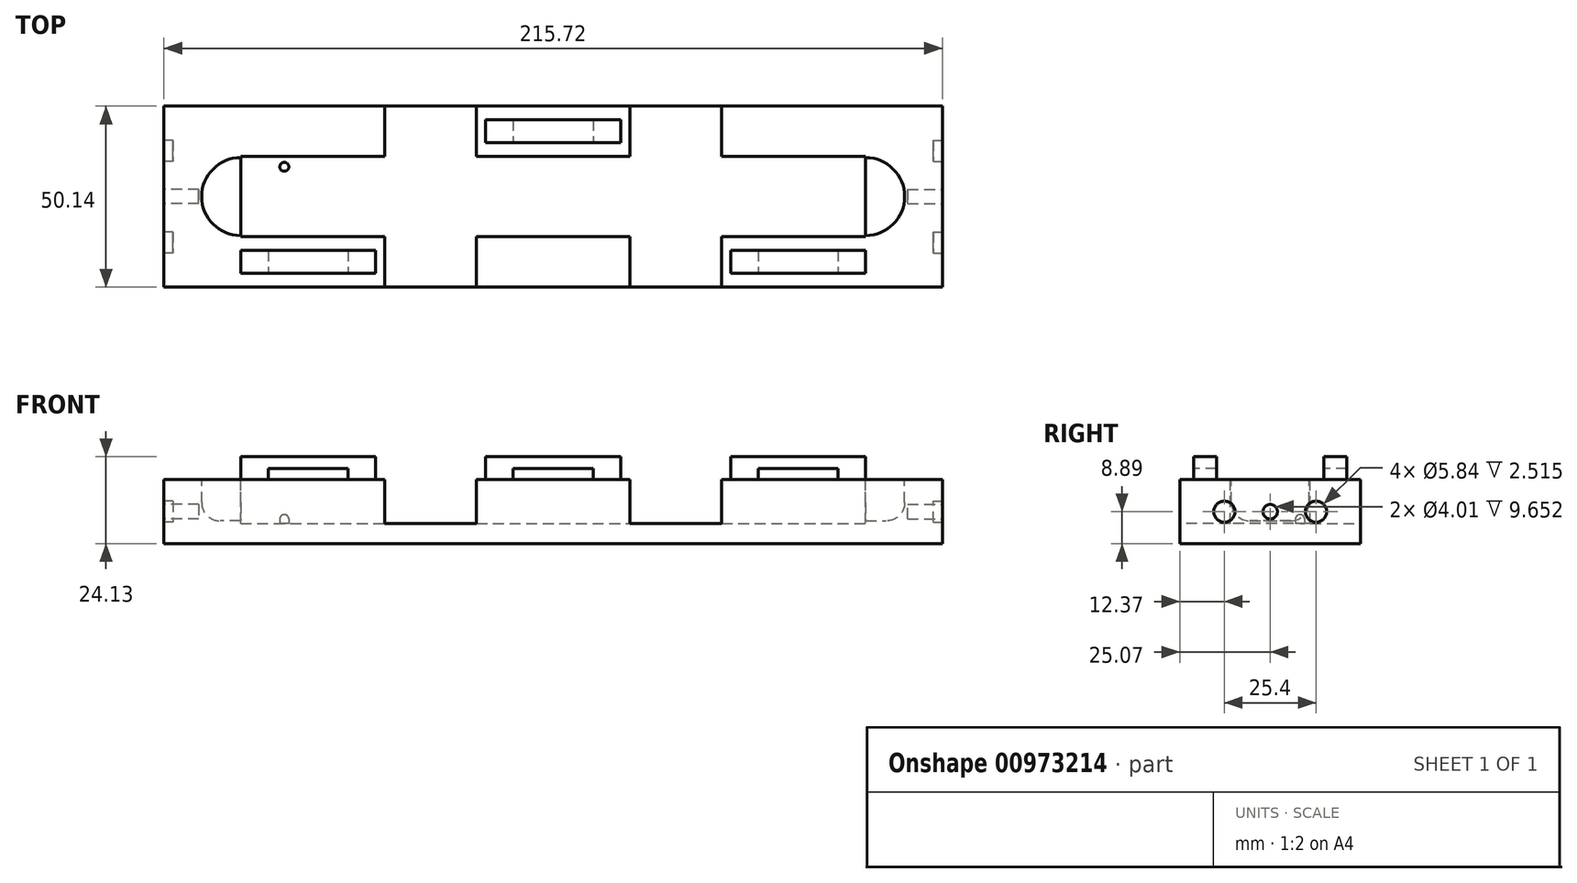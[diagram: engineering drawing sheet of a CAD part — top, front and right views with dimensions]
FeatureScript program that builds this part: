
annotation { "Feature Type Name" : "Feature", "Feature Type Description" : "" }
export const myFeature = defineFeature(function(context is Context, id is Id, definition is map)
    precondition{}
    {
        {
            var Q0;
            Q0=qCreatedBy(makeId("Top.planeOp"),FACE);
            var sketch = newSketch(context, id + "F0", { "sketchPlane" : qUnion([Q0])});
            skLineSegment(sketch, "E0.bottom", {"start": v(-107.86, 25.07) * mm, "end": v(107.86, 25.07) * mm});
            skLineSegment(sketch, "E0.top", {"start": v(-107.86, -25.07) * mm, "end": v(107.86, -25.07) * mm});
            skLineSegment(sketch, "E0.left", {"start": v(-107.86, 25.07) * mm, "end": v(-107.86, -25.07) * mm});
            skLineSegment(sketch, "E0.right", {"start": v(107.86, 25.07) * mm, "end": v(107.86, -25.07) * mm});
            skPoint(sketch, "E0.middle", {"position": v(0, 0) * mm});
            skSolve(sketch);
        }
        {
            var Q0;
            Q0=makeQuery(id+"F0.imprint","IMPRINT",FACE,{"disambiguationData":[TD([[makeQuery(id+"F0.imprint","IMPRINT",EDGE,{"derivedFrom":sQuery(id+"F0.wireOp",EDGE,"E0.bottom")}),-1.0]])]});
            extrude(context, id + "F1", {"entities" : qUnion([Q0]), "depth" : 17.78 * mm, "offsetDistance" : 25.4 * mm});
        }
        {
            var Q0;
            Q0=makeQuery(id+"F1.opExtrude","CAP_FACE",FACE,{"disambiguationData":[OSD([sQuery(id+"F0.wireOp",EDGE,"E0.bottom"),sQuery(id+"F0.wireOp",EDGE,"E0.top"),sQuery(id+"F0.wireOp",EDGE,"E0.left"),sQuery(id+"F0.wireOp",EDGE,"E0.right")])],"isStart":false});
            var sketch = newSketch(context, id + "F2", { "sketchPlane" : qUnion([Q0])});
            skLineSegment(sketch, "E1.bottom", {"start": v(-86.6, 11.1) * mm, "end": v(86.6, 11.1) * mm});
            skLineSegment(sketch, "E1.top", {"start": v(-86.6, -11.1) * mm, "end": v(86.6, -11.1) * mm});
            skLineSegment(sketch, "E1.left", {"start": v(-86.6, 11.1) * mm, "end": v(-86.6, -11.1) * mm});
            skLineSegment(sketch, "E1.right", {"start": v(86.6, 11.1) * mm, "end": v(86.6, -11.1) * mm});
            skPoint(sketch, "E1.middle", {"position": v(0, 0) * mm});
            skSolve(sketch);
        }
        {
            var Q0;
            Q0=makeQuery(id+"F2.imprint","IMPRINT",FACE,{"disambiguationData":[TD([[makeQuery(id+"F2.imprint","IMPRINT",EDGE,{"derivedFrom":sQuery(id+"F2.wireOp",EDGE,"E1.bottom")}),-1.0]])]});
            extrude(context, id + "F3", {"entities" : qUnion([Q0]), "operationType" : NewBodyOperationType.REMOVE, "oppositeDirection" : true, "depth" : 12.2 * mm, "offsetDistance" : 25.4 * mm});
        }
        {
            var Q0;
            Q0=makeQuery(id+"F1.opExtrude","CAP_FACE",FACE,{"disambiguationData":[OSD([sQuery(id+"F0.wireOp",EDGE,"E0.bottom"),sQuery(id+"F0.wireOp",EDGE,"E0.top"),sQuery(id+"F0.wireOp",EDGE,"E0.left"),sQuery(id+"F0.wireOp",EDGE,"E0.right")])],"isStart":false});
            var sketch = newSketch(context, id + "F4", { "sketchPlane" : qUnion([Q0])});
            skCircle(sketch, "E2", {"center": v(-86.6, 0) * mm, "radius": 10.8 * mm});
            skCircle(sketch, "E3", {"center": v(86.6, 0) * mm, "radius": 10.8 * mm});
            skSolve(sketch);
        }
        {
            var Q0;
            {var subQ0=sQuery(id+"F4.wireOp",EDGE,"E2");var subQ1=makeQuery(id+"F3.boolean.opBoolean","COPY",EDGE,{"derivedFrom":makeQuery(id+"F3.opExtrude","CAP_EDGE",EDGE,{"disambiguationData":[OSD([sQuery(id+"F2.wireOp",EDGE,"E1.left")])],"isStart":true})});var subQ2=makeQuery(id+"F4.imprint","INTERSECT",VERTEX,{"disambiguationData":[OD(0.0)],"derivedFrom":[subQ1,subQ0]});Q0=makeQuery(id+"F4.imprint","IMPRINT",FACE,{"disambiguationData":[TD([[makeQuery(id+"F4.imprint","IMPRINT",EDGE,{"disambiguationData":[TD([[subQ2,-1.0]])],"derivedFrom":subQ0}),1.0]])]});}
            var Q1;
            {var subQ0=sQuery(id+"F4.wireOp",EDGE,"7IIQq3Zt-Aci2-6bUa-GBsR-gUbxx56y20vS");var subQ1=makeQuery(id+"F3.boolean.opBoolean","COPY",EDGE,{"derivedFrom":makeQuery(id+"F3.opExtrude","CAP_EDGE",EDGE,{"disambiguationData":[OSD([sQuery(id+"F2.wireOp",EDGE,"E1.bottom")])],"isStart":true})});var subQ2=makeQuery(id+"F4.imprint","INTERSECT",VERTEX,{"disambiguationData":[OD(0.0)],"derivedFrom":[subQ1,subQ0]});Q1=makeQuery(id+"F4.imprint","IMPRINT",FACE,{"disambiguationData":[TD([[makeQuery(id+"F4.imprint","IMPRINT",EDGE,{"disambiguationData":[TD([[subQ2,1.0]])],"derivedFrom":subQ0}),1.0]])]});}
            var Q2;
            {var subQ0=sQuery(id+"F4.wireOp",EDGE,"ctRysrec-sLNG-mFqm-rWU9-T6cm6gCdLbKU");var subQ1=makeQuery(id+"F3.boolean.opBoolean","COPY",EDGE,{"derivedFrom":makeQuery(id+"F3.opExtrude","CAP_EDGE",EDGE,{"disambiguationData":[OSD([sQuery(id+"F2.wireOp",EDGE,"E1.top")])],"isStart":true})});var subQ2=makeQuery(id+"F4.imprint","INTERSECT",VERTEX,{"disambiguationData":[OD(0.0)],"derivedFrom":[subQ1,subQ0]});Q2=makeQuery(id+"F4.imprint","IMPRINT",FACE,{"disambiguationData":[TD([[makeQuery(id+"F4.imprint","IMPRINT",EDGE,{"disambiguationData":[TD([[subQ2,1.0]])],"derivedFrom":subQ0}),1.0]])]});}
            var Q3;
            {var subQ0=sQuery(id+"F4.wireOp",EDGE,"WosAOIdG-twBO-UutL-H2nZ-O1rzlQHSEw63");var subQ1=makeQuery(id+"F3.boolean.opBoolean","COPY",EDGE,{"derivedFrom":makeQuery(id+"F3.opExtrude","CAP_EDGE",EDGE,{"disambiguationData":[OSD([sQuery(id+"F2.wireOp",EDGE,"E1.bottom")])],"isStart":true})});var subQ2=makeQuery(id+"F4.imprint","INTERSECT",VERTEX,{"disambiguationData":[OD(0.0)],"derivedFrom":[subQ1,subQ0]});Q3=makeQuery(id+"F4.imprint","IMPRINT",FACE,{"disambiguationData":[TD([[makeQuery(id+"F4.imprint","IMPRINT",EDGE,{"disambiguationData":[TD([[subQ2,1.0]])],"derivedFrom":subQ0}),1.0]])]});}
            var Q4;
            {var subQ0=sQuery(id+"F4.wireOp",EDGE,"E3");var subQ1=makeQuery(id+"F3.boolean.opBoolean","COPY",EDGE,{"derivedFrom":makeQuery(id+"F3.opExtrude","CAP_EDGE",EDGE,{"disambiguationData":[OSD([sQuery(id+"F2.wireOp",EDGE,"E1.right")])],"isStart":true})});var subQ2=makeQuery(id+"F4.imprint","INTERSECT",VERTEX,{"disambiguationData":[OD(0.0)],"derivedFrom":[subQ1,subQ0]});Q4=makeQuery(id+"F4.imprint","IMPRINT",FACE,{"disambiguationData":[TD([[makeQuery(id+"F4.imprint","IMPRINT",EDGE,{"disambiguationData":[TD([[subQ2,1.0]])],"derivedFrom":subQ0}),1.0]])]});}
            var Q5;
            {var subQ0=sQuery(id+"F4.wireOp",EDGE,"np94UB7D-fCDP-aEEe-Vjp5-RGfSFigQMC2d");var subQ1=makeQuery(id+"F3.boolean.opBoolean","COPY",EDGE,{"derivedFrom":makeQuery(id+"F3.opExtrude","CAP_EDGE",EDGE,{"disambiguationData":[OSD([sQuery(id+"F2.wireOp",EDGE,"E1.top")])],"isStart":true})});var subQ2=makeQuery(id+"F4.imprint","INTERSECT",VERTEX,{"disambiguationData":[OD(0.0)],"derivedFrom":[subQ1,subQ0]});Q5=makeQuery(id+"F4.imprint","IMPRINT",FACE,{"disambiguationData":[TD([[makeQuery(id+"F4.imprint","IMPRINT",EDGE,{"disambiguationData":[TD([[subQ2,1.0]])],"derivedFrom":subQ0}),1.0]])]});}
            extrude(context, id + "F5", {"entities" : qUnion([Q0, Q1, Q2, Q3, Q4, Q5]), "operationType" : NewBodyOperationType.REMOVE, "oppositeDirection" : true, "depth" : 11.43 * mm, "offsetDistance" : 25.4 * mm});
        }
        {
            var Q0;
            Q0=makeQuery(id+"F5.boolean.opBoolean","COPY",EDGE,{"derivedFrom":makeQuery(id+"F5.opExtrude","CAP_EDGE",EDGE,{"disambiguationData":[OSD([sQuery(id+"F4.wireOp",EDGE,"E2")])],"isStart":false})});
            var Q1;
            Q1=makeQuery(id+"F5.boolean.opBoolean","COPY",EDGE,{"derivedFrom":makeQuery(id+"F5.opExtrude","CAP_EDGE",EDGE,{"disambiguationData":[OSD([sQuery(id+"F4.wireOp",EDGE,"7IIQq3Zt-Aci2-6bUa-GBsR-gUbxx56y20vS")])],"isStart":false})});
            var Q2;
            Q2=makeQuery(id+"F5.boolean.opBoolean","COPY",EDGE,{"derivedFrom":makeQuery(id+"F5.opExtrude","CAP_EDGE",EDGE,{"disambiguationData":[OSD([sQuery(id+"F4.wireOp",EDGE,"ctRysrec-sLNG-mFqm-rWU9-T6cm6gCdLbKU")])],"isStart":false})});
            var Q3;
            Q3=makeQuery(id+"F5.boolean.opBoolean","COPY",EDGE,{"derivedFrom":makeQuery(id+"F5.opExtrude","CAP_EDGE",EDGE,{"disambiguationData":[OSD([sQuery(id+"F4.wireOp",EDGE,"WosAOIdG-twBO-UutL-H2nZ-O1rzlQHSEw63")])],"isStart":false})});
            var Q4;
            Q4=makeQuery(id+"F5.boolean.opBoolean","COPY",EDGE,{"derivedFrom":makeQuery(id+"F5.opExtrude","CAP_EDGE",EDGE,{"disambiguationData":[OSD([sQuery(id+"F4.wireOp",EDGE,"E3")])],"isStart":false})});
            var Q5;
            Q5=makeQuery(id+"F5.boolean.opBoolean","COPY",EDGE,{"derivedFrom":makeQuery(id+"F5.opExtrude","CAP_EDGE",EDGE,{"disambiguationData":[OSD([sQuery(id+"F4.wireOp",EDGE,"np94UB7D-fCDP-aEEe-Vjp5-RGfSFigQMC2d")])],"isStart":false})});
            fillet(context, id + "F6", {"entities" : qUnion([Q0, Q1, Q2, Q3, Q4, Q5]), "radius" : 5.08 * mm, "tangentPropagation" : true, "allowEdgeOverflow" : false});
        }
        {
            var Q0;
            Q0=makeQuery(id+"F3.boolean.opBoolean","COPY",FACE,{"derivedFrom":makeQuery(id+"F3.opExtrude","CAP_FACE",FACE,{"disambiguationData":[OSD([sQuery(id+"F2.wireOp",EDGE,"E1.bottom"),sQuery(id+"F2.wireOp",EDGE,"E1.top"),sQuery(id+"F2.wireOp",EDGE,"E1.left"),sQuery(id+"F2.wireOp",EDGE,"E1.right")])],"isStart":false})});
            var sketch = newSketch(context, id + "F7", { "sketchPlane" : qUnion([Q0])});
            skLineSegment(sketch, "E4.bottom", {"start": v(0, 11.1) * mm, "end": v(-74.5, 11.1) * mm});
            skLineSegment(sketch, "E4.top", {"start": v(0, 8.26) * mm, "end": v(-74.5, 8.25) * mm});
            skLineSegment(sketch, "E4.left", {"start": v(0, 11.1) * mm, "end": v(0, 8.26) * mm});
            skLineSegment(sketch, "E4.right", {"start": v(-74.5, 11.1) * mm, "end": v(-74.5, 8.25) * mm});
            skCircle(sketch, "E5", {"center": v(-74.5, 8.25) * mm, "radius": 1.24 * mm});
            skSolve(sketch);
        }
        {
            var Q0;
            {var subQ0=sQuery(id+"F7.wireOp",EDGE,"E4.right");var subQ1=sQuery(id+"F7.wireOp",EDGE,"E4.top");var subQ2=makeQuery(id+"F7.imprint","INTERSECT",VERTEX,{"derivedFrom":[subQ1,subQ0]});Q0=makeQuery(id+"F7.imprint","IMPRINT",FACE,{"disambiguationData":[TD([[makeQuery(id+"F7.imprint","IMPRINT",EDGE,{"disambiguationData":[TD([[subQ2,1.0]])],"derivedFrom":subQ1}),1.0]])]});}
            var Q1;
            {var subQ0=sQuery(id+"F7.wireOp",EDGE,"E4.right");var subQ1=sQuery(id+"F7.wireOp",EDGE,"E4.top");var subQ2=makeQuery(id+"F7.imprint","INTERSECT",VERTEX,{"derivedFrom":[subQ1,subQ0]});Q1=makeQuery(id+"F7.imprint","IMPRINT",FACE,{"disambiguationData":[TD([[makeQuery(id+"F7.imprint","IMPRINT",EDGE,{"disambiguationData":[TD([[subQ2,1.0]])],"derivedFrom":subQ1}),-1.0]])]});}
            extrude(context, id + "F8", {"entities" : qUnion([Q0, Q1]), "operationType" : NewBodyOperationType.ADD, "depth" : 2.5 * mm, "offsetDistance" : 25.4 * mm});
        }
        {
            var Q0;
            Q0=makeQuery(id+"F8.opExtrude","CAP_FACE",FACE,{"disambiguationData":[OSD([sQuery(id+"F7.wireOp",EDGE,"E5")])],"isStart":false});
            fillet(context, id + "F9", {"entities" : qUnion([Q0]), "radius" : 1.24 * mm, "tangentPropagation" : true, "allowEdgeOverflow" : false});
        }
        {
            var Q0;
            Q0=makeQuery(id+"F1.opExtrude","SWEPT_FACE",FACE,{"disambiguationData":[OSD([sQuery(id+"F0.wireOp",EDGE,"E0.right")])]});
            var sketch = newSketch(context, id + "F10", { "sketchPlane" : qUnion([Q0])});
            skCircle(sketch, "E6", {"center": v(0, 8.9) * mm, "radius": 2 * mm});
            skPoint(sketch, "E6.centerSnap0", {"position": v(0, 17.78) * mm});
            skSolve(sketch);
        }
        {
            var Q0;
            Q0=makeQuery(id+"F10.imprint","IMPRINT",FACE,{"disambiguationData":[TD([[makeQuery(id+"F10.imprint","IMPRINT",EDGE,{"derivedFrom":sQuery(id+"F10.wireOp",EDGE,"E6")}),1.0]])]});
            extrude(context, id + "F11", {"entities" : qUnion([Q0]), "operationType" : NewBodyOperationType.REMOVE, "oppositeDirection" : true, "depth" : 9.65 * mm, "offsetDistance" : 25.4 * mm});
        }
        {
            var Q0;
            Q0=makeQuery(id+"F1.opExtrude","SWEPT_FACE",FACE,{"disambiguationData":[OSD([sQuery(id+"F0.wireOp",EDGE,"E0.left")])]});
            var sketch = newSketch(context, id + "F12", { "sketchPlane" : qUnion([Q0])});
            skCircle(sketch, "E7", {"center": v(0, 8.9) * mm, "radius": 2 * mm});
            skSolve(sketch);
        }
        {
            var Q0;
            Q0=makeQuery(id+"F12.imprint","IMPRINT",FACE,{"disambiguationData":[TD([[makeQuery(id+"F12.imprint","IMPRINT",EDGE,{"derivedFrom":sQuery(id+"F12.wireOp",EDGE,"E7")}),1.0]])]});
            extrude(context, id + "F13", {"entities" : qUnion([Q0]), "operationType" : NewBodyOperationType.REMOVE, "oppositeDirection" : true, "depth" : 9.65 * mm, "offsetDistance" : 25.4 * mm});
        }
        {
            var Q0;
            Q0=makeQuery(id+"F1.opExtrude","SWEPT_FACE",FACE,{"disambiguationData":[OSD([sQuery(id+"F0.wireOp",EDGE,"E0.right")])]});
            var sketch = newSketch(context, id + "F14", { "sketchPlane" : qUnion([Q0])});
            skCircle(sketch, "E8", {"center": v(-12.7, 8.9) * mm, "radius": 2.92 * mm});
            skPoint(sketch, "E8.centerSnap0", {"position": v(-25.07, 8.9) * mm});
            skCircle(sketch, "E9", {"center": v(12.7, 8.9) * mm, "radius": 2.92 * mm});
            skPoint(sketch, "E9.centerSnap0", {"position": v(25.07, 8.9) * mm});
            skSolve(sketch);
        }
        {
            var Q0;
            Q0=makeQuery(id+"F14.imprint","IMPRINT",FACE,{"disambiguationData":[TD([[makeQuery(id+"F14.imprint","IMPRINT",EDGE,{"derivedFrom":sQuery(id+"F14.wireOp",EDGE,"E8")}),1.0]])]});
            var Q1;
            Q1=makeQuery(id+"F14.imprint","IMPRINT",FACE,{"disambiguationData":[TD([[makeQuery(id+"F14.imprint","IMPRINT",EDGE,{"derivedFrom":sQuery(id+"F14.wireOp",EDGE,"E9")}),1.0]])]});
            extrude(context, id + "F15", {"entities" : qUnion([Q0, Q1]), "operationType" : NewBodyOperationType.REMOVE, "oppositeDirection" : true, "depth" : 2.5 * mm, "offsetDistance" : 25.4 * mm});
        }
        {
            var Q0;
            Q0=makeQuery(id+"F1.opExtrude","SWEPT_FACE",FACE,{"disambiguationData":[OSD([sQuery(id+"F0.wireOp",EDGE,"E0.left")])]});
            var sketch = newSketch(context, id + "F16", { "sketchPlane" : qUnion([Q0])});
            skCircle(sketch, "E10", {"center": v(-12.7, 8.9) * mm, "radius": 2.92 * mm});
            skCircle(sketch, "E11", {"center": v(12.7, 8.9) * mm, "radius": 2.92 * mm});
            skPoint(sketch, "E11.centerSnap0", {"position": v(-25.07, 8.9) * mm});
            skSolve(sketch);
        }
        {
            var Q0;
            Q0=makeQuery(id+"F16.imprint","IMPRINT",FACE,{"disambiguationData":[TD([[makeQuery(id+"F16.imprint","IMPRINT",EDGE,{"derivedFrom":sQuery(id+"F16.wireOp",EDGE,"E10")}),1.0]])]});
            var Q1;
            Q1=makeQuery(id+"F16.imprint","IMPRINT",FACE,{"disambiguationData":[TD([[makeQuery(id+"F16.imprint","IMPRINT",EDGE,{"derivedFrom":sQuery(id+"F16.wireOp",EDGE,"E11")}),1.0]])]});
            extrude(context, id + "F17", {"entities" : qUnion([Q0, Q1]), "operationType" : NewBodyOperationType.REMOVE, "oppositeDirection" : true, "depth" : 2.5 * mm, "offsetDistance" : 25.4 * mm});
        }
        {
            var Q0;
            Q0=makeQuery(id+"F1.opExtrude","CAP_FACE",FACE,{"disambiguationData":[OSD([sQuery(id+"F0.wireOp",EDGE,"E0.bottom"),sQuery(id+"F0.wireOp",EDGE,"E0.top"),sQuery(id+"F0.wireOp",EDGE,"E0.left"),sQuery(id+"F0.wireOp",EDGE,"E0.right")])],"isStart":false});
            var sketch = newSketch(context, id + "F18", { "sketchPlane" : qUnion([Q0])});
            skLineSegment(sketch, "E12.bottom", {"start": v(-18.72, 21.26) * mm, "end": v(18.72, 21.26) * mm});
            skLineSegment(sketch, "E12.top", {"start": v(-18.72, 14.9) * mm, "end": v(18.72, 14.9) * mm});
            skLineSegment(sketch, "E12.left", {"start": v(-18.72, 21.26) * mm, "end": v(-18.72, 14.9) * mm});
            skLineSegment(sketch, "E12.right", {"start": v(18.72, 21.26) * mm, "end": v(18.72, 14.9) * mm});
            skPoint(sketch, "E12.middle", {"position": v(0, 18.08) * mm});
            skSolve(sketch);
        }
        {
            var Q0;
            Q0=makeQuery(id+"F18.imprint","IMPRINT",FACE,{"disambiguationData":[TD([[makeQuery(id+"F18.imprint","IMPRINT",EDGE,{"derivedFrom":sQuery(id+"F18.wireOp",EDGE,"E12.bottom")}),-1.0]])]});
            extrude(context, id + "F19", {"entities" : qUnion([Q0]), "operationType" : NewBodyOperationType.ADD, "depth" : 6.35 * mm, "offsetDistance" : 25.4 * mm});
        }
        {
            var Q0;
            Q0=makeQuery(id+"F1.opExtrude","CAP_FACE",FACE,{"disambiguationData":[OSD([sQuery(id+"F0.wireOp",EDGE,"E0.bottom"),sQuery(id+"F0.wireOp",EDGE,"E0.top"),sQuery(id+"F0.wireOp",EDGE,"E0.left"),sQuery(id+"F0.wireOp",EDGE,"E0.right")])],"isStart":false});
            var sketch = newSketch(context, id + "F20", { "sketchPlane" : qUnion([Q0])});
            skLineSegment(sketch, "E13.bottom", {"start": v(-49.16, -21.26) * mm, "end": v(-86.6, -21.26) * mm});
            skLineSegment(sketch, "E13.top", {"start": v(-49.16, -14.9) * mm, "end": v(-86.6, -14.9) * mm});
            skLineSegment(sketch, "E13.left", {"start": v(-49.16, -21.26) * mm, "end": v(-49.16, -14.9) * mm});
            skLineSegment(sketch, "E13.right", {"start": v(-86.6, -21.26) * mm, "end": v(-86.6, -14.9) * mm});
            skPoint(sketch, "E13.middle", {"position": v(-67.88, -18.08) * mm});
            skLineSegment(sketch, "E14.bottom", {"start": v(49.16, -21.26) * mm, "end": v(86.6, -21.26) * mm});
            skLineSegment(sketch, "E14.top", {"start": v(49.16, -14.9) * mm, "end": v(86.6, -14.9) * mm});
            skLineSegment(sketch, "E14.left", {"start": v(49.16, -21.26) * mm, "end": v(49.16, -14.9) * mm});
            skLineSegment(sketch, "E14.right", {"start": v(86.6, -21.26) * mm, "end": v(86.6, -14.9) * mm});
            skPoint(sketch, "E14.middle", {"position": v(67.88, -18.08) * mm});
            skSolve(sketch);
        }
        {
            var Q0;
            Q0 = qSketchRegion(id + "F20", true);
            extrude(context, id + "F21", {"entities" : qUnion([Q0]), "operationType" : NewBodyOperationType.ADD, "depth" : 6.35 * mm, "offsetDistance" : 25.4 * mm});
        }
        {
            var Q0;
            Q0=makeQuery(id+"F21.opExtrude","SWEPT_FACE",FACE,{"disambiguationData":[OSD([sQuery(id+"F20.wireOp",EDGE,"E13.bottom")])]});
            var sketch = newSketch(context, id + "F22", { "sketchPlane" : qUnion([Q0])});
            skLineSegment(sketch, "E15.bottom", {"start": v(-78.98, 17.78) * mm, "end": v(-56.78, 17.78) * mm});
            skLineSegment(sketch, "E15.top", {"start": v(-78.98, 20.83) * mm, "end": v(-56.78, 20.83) * mm});
            skLineSegment(sketch, "E15.left", {"start": v(-78.98, 17.78) * mm, "end": v(-78.98, 20.83) * mm});
            skLineSegment(sketch, "E15.right", {"start": v(-56.78, 17.78) * mm, "end": v(-56.78, 20.83) * mm});
            skSolve(sketch);
        }
        {
            var Q0;
            Q0=makeQuery(id+"F19.opExtrude","SWEPT_FACE",FACE,{"disambiguationData":[OSD([sQuery(id+"F18.wireOp",EDGE,"E12.top")])]});
            var sketch = newSketch(context, id + "F23", { "sketchPlane" : qUnion([Q0])});
            skLineSegment(sketch, "E16.bottom", {"start": v(-11.1, 17.78) * mm, "end": v(11.1, 17.78) * mm});
            skLineSegment(sketch, "E16.top", {"start": v(-11.1, 20.83) * mm, "end": v(11.1, 20.83) * mm});
            skLineSegment(sketch, "E16.left", {"start": v(-11.1, 17.78) * mm, "end": v(-11.1, 20.83) * mm});
            skLineSegment(sketch, "E16.right", {"start": v(11.1, 17.78) * mm, "end": v(11.1, 20.83) * mm});
            skSolve(sketch);
        }
        {
            var Q0;
            Q0=makeQuery(id+"F21.opExtrude","SWEPT_FACE",FACE,{"disambiguationData":[OSD([sQuery(id+"F20.wireOp",EDGE,"E14.bottom")])]});
            var sketch = newSketch(context, id + "F24", { "sketchPlane" : qUnion([Q0])});
            skLineSegment(sketch, "E17.bottom", {"start": v(56.78, 17.78) * mm, "end": v(78.98, 17.78) * mm});
            skLineSegment(sketch, "E17.top", {"start": v(56.78, 20.83) * mm, "end": v(78.98, 20.83) * mm});
            skLineSegment(sketch, "E17.left", {"start": v(56.78, 17.78) * mm, "end": v(56.78, 20.83) * mm});
            skLineSegment(sketch, "E17.right", {"start": v(78.98, 17.78) * mm, "end": v(78.98, 20.83) * mm});
            skSolve(sketch);
        }
        {
            var Q0;
            Q0=makeQuery(id+"F24.imprint","IMPRINT",FACE,{"disambiguationData":[TD([[makeQuery(id+"F24.imprint","IMPRINT",EDGE,{"derivedFrom":sQuery(id+"F24.wireOp",EDGE,"E17.bottom")}),1.0]])]});
            var Q1;
            Q1=makeQuery(id+"F23.imprint","IMPRINT",FACE,{"disambiguationData":[TD([[makeQuery(id+"F23.imprint","IMPRINT",EDGE,{"derivedFrom":sQuery(id+"F23.wireOp",EDGE,"E16.bottom")}),1.0]])]});
            var Q2;
            Q2=makeQuery(id+"F22.imprint","IMPRINT",FACE,{"disambiguationData":[TD([[makeQuery(id+"F22.imprint","IMPRINT",EDGE,{"derivedFrom":sQuery(id+"F22.wireOp",EDGE,"E15.bottom")}),-1.0]])]});
            extrude(context, id + "F25", {"entities" : qUnion([Q0, Q1, Q2]), "operationType" : NewBodyOperationType.REMOVE, "oppositeDirection" : true, "depth" : 7.62 * mm, "offsetDistance" : 25.4 * mm});
        }
        {
            var Q0;
            Q0=makeQuery(id+"F25.boolean.opBoolean","MERGE",FACE,{"derivedFrom":[makeQuery(id+"F1.opExtrude","CAP_FACE",FACE,{"disambiguationData":[OSD([sQuery(id+"F0.wireOp",EDGE,"E0.bottom"),sQuery(id+"F0.wireOp",EDGE,"E0.top"),sQuery(id+"F0.wireOp",EDGE,"E0.left"),sQuery(id+"F0.wireOp",EDGE,"E0.right")])],"isStart":false})],"fromTools":[makeQuery(id+"F25.opExtrude","SWEPT_FACE",FACE,{"disambiguationData":[OSD([sQuery(id+"F22.wireOp",EDGE,"E15.bottom")])]}),makeQuery(id+"F25.opExtrude","SWEPT_FACE",FACE,{"disambiguationData":[OSD([sQuery(id+"F23.wireOp",EDGE,"E16.bottom")])]}),makeQuery(id+"F25.opExtrude","SWEPT_FACE",FACE,{"disambiguationData":[OSD([sQuery(id+"F24.wireOp",EDGE,"E17.bottom")])]})]});
            var sketch = newSketch(context, id + "F26", { "sketchPlane" : qUnion([Q0])});
            skLineSegment(sketch, "E18.bottom", {"start": v(-46.66, 11.1) * mm, "end": v(-21.26, 11.1) * mm});
            skLineSegment(sketch, "E18.top", {"start": v(-46.66, 25.07) * mm, "end": v(-21.26, 25.07) * mm});
            skLineSegment(sketch, "E18.left", {"start": v(-46.66, 11.1) * mm, "end": v(-46.66, 25.07) * mm});
            skLineSegment(sketch, "E18.right", {"start": v(-21.26, 11.1) * mm, "end": v(-21.26, 25.07) * mm});
            skLineSegment(sketch, "E19.bottom", {"start": v(-46.66, -11.1) * mm, "end": v(-21.26, -11.1) * mm});
            skLineSegment(sketch, "E19.top", {"start": v(-46.66, -25.07) * mm, "end": v(-21.26, -25.07) * mm});
            skLineSegment(sketch, "E19.left", {"start": v(-46.66, -11.1) * mm, "end": v(-46.66, -25.07) * mm});
            skLineSegment(sketch, "E19.right", {"start": v(-21.26, -11.1) * mm, "end": v(-21.26, -25.07) * mm});
            skLineSegment(sketch, "E20.bottom", {"start": v(21.26, 11.1) * mm, "end": v(46.66, 11.1) * mm});
            skLineSegment(sketch, "E20.top", {"start": v(21.26, 25.07) * mm, "end": v(46.66, 25.07) * mm});
            skLineSegment(sketch, "E20.left", {"start": v(21.26, 11.1) * mm, "end": v(21.26, 25.07) * mm});
            skLineSegment(sketch, "E20.right", {"start": v(46.66, 11.1) * mm, "end": v(46.66, 25.07) * mm});
            skLineSegment(sketch, "E21.bottom", {"start": v(21.26, -11.1) * mm, "end": v(46.66, -11.1) * mm});
            skLineSegment(sketch, "E21.top", {"start": v(21.26, -25.07) * mm, "end": v(46.66, -25.07) * mm});
            skLineSegment(sketch, "E21.left", {"start": v(21.26, -11.1) * mm, "end": v(21.26, -25.07) * mm});
            skLineSegment(sketch, "E21.right", {"start": v(46.66, -11.1) * mm, "end": v(46.66, -25.07) * mm});
            skSolve(sketch);
        }
        {
            var Q0;
            Q0=makeQuery(id+"F26.imprint","IMPRINT",FACE,{"disambiguationData":[TD([[makeQuery(id+"F26.imprint","IMPRINT",EDGE,{"derivedFrom":sQuery(id+"F26.wireOp",EDGE,"E18.bottom")}),1.0]])]});
            var Q1;
            Q1=makeQuery(id+"F26.imprint","IMPRINT",FACE,{"disambiguationData":[TD([[makeQuery(id+"F26.imprint","IMPRINT",EDGE,{"derivedFrom":sQuery(id+"F26.wireOp",EDGE,"E19.bottom")}),-1.0]])]});
            var Q2;
            Q2=makeQuery(id+"F26.imprint","IMPRINT",FACE,{"disambiguationData":[TD([[makeQuery(id+"F26.imprint","IMPRINT",EDGE,{"derivedFrom":sQuery(id+"F26.wireOp",EDGE,"E21.bottom")}),-1.0]])]});
            var Q3;
            Q3=makeQuery(id+"F26.imprint","IMPRINT",FACE,{"disambiguationData":[TD([[makeQuery(id+"F26.imprint","IMPRINT",EDGE,{"derivedFrom":sQuery(id+"F26.wireOp",EDGE,"E20.bottom")}),1.0]])]});
            extrude(context, id + "F27", {"entities" : qUnion([Q0, Q1, Q2, Q3]), "operationType" : NewBodyOperationType.REMOVE, "oppositeDirection" : true, "depth" : 12.2 * mm, "offsetDistance" : 25.4 * mm});
        }
    });
